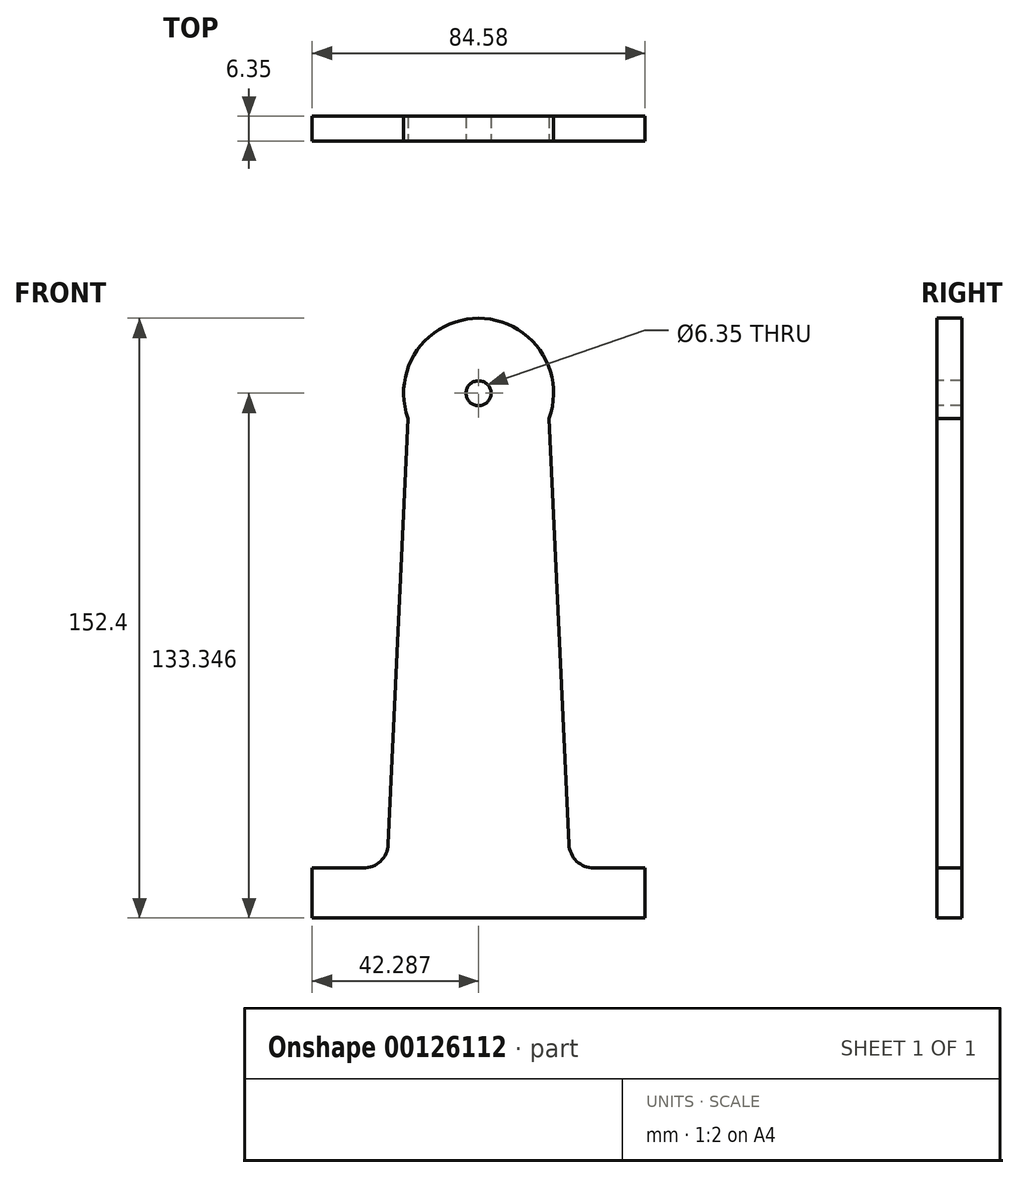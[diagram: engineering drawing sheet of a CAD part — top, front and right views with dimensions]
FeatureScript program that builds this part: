
annotation { "Feature Type Name" : "Feature", "Feature Type Description" : "" }
export const myFeature = defineFeature(function(context is Context, id is Id, definition is map)
    precondition{}
    {
        {
            var Q0;
            Q0=qCreatedBy(makeId("Front.planeOp"),FACE);
            var sketch = newSketch(context, id + "F0", { "sketchPlane" : qUnion([Q0])});
            skLineSegment(sketch, "E0", {"start": v(-71.6, -84.21) * mm, "end": v(12.99, -84.21) * mm});
            skLineSegment(sketch, "E1", {"start": v(12.99, -84.21) * mm, "end": v(12.99, -71.51) * mm});
            skLineSegment(sketch, "E2", {"start": v(12.99, -71.51) * mm, "end": v(0, -71.51) * mm});
            skLineSegment(sketch, "E3", {"start": v(-71.6, -84.21) * mm, "end": v(-71.6, -71.51) * mm});
            skLineSegment(sketch, "E4", {"start": v(-71.6, -71.51) * mm, "end": v(-58.6, -71.51) * mm});
            skPoint(sketch, "E5.endSnap0", {"position": v(-29.3, -84.21) * mm});
            skLineSegment(sketch, "E6", {"start": v(-29.3, -84.21) * mm, "end": v(-29.3, 49.14) * mm, "construction": true});
            skCircle(sketch, "E7", {"center": v(-29.3, 49.14) * mm, "radius": 19.05 * mm});
            skLineSegment(sketch, "E8", {"start": v(-29.3, 49.14) * mm, "end": v(-29.3, 68.19) * mm, "construction": true});
            skLineSegment(sketch, "E9", {"start": v(-6.34, -65.46) * mm, "end": v(-11.36, 42.74) * mm});
            skLineSegment(sketch, "E10", {"start": v(-52.26, -65.46) * mm, "end": v(-47.25, 42.74) * mm});
            skPoint(sketch, "E11.visualSharp", {"position": v(-52.54, -71.51) * mm});
            skArc(sketch, "E11.filletArc", {"start": v(-58.6, -71.51) * mm, "mid": v(-54.22, -69.76) * mm, "end": v(-52.26, -65.46) * mm});
            skPoint(sketch, "E12.visualSharp", {"position": v(-6.06, -71.51) * mm});
            skArc(sketch, "E12.filletArc", {"start": v(-6.34, -65.46) * mm, "mid": v(-4.38, -69.76) * mm, "end": v(0, -71.51) * mm});
            skCircle(sketch, "E13", {"center": v(-29.3, 49.14) * mm, "radius": 3.18 * mm});
            skSolve(sketch);
        }
        {
            var Q0;
            Q0=makeQuery(id+"F0.imprint","IMPRINT",FACE,{"disambiguationData":[TD([[makeQuery(id+"F0.imprint","IMPRINT",EDGE,{"derivedFrom":sQuery(id+"F0.wireOp",EDGE,"E0")}),1.0]])]});
            var Q1;
            Q1=makeQuery(id+"F0.imprint","IMPRINT",FACE,{"disambiguationData":[TD([[makeQuery(id+"F0.imprint","IMPRINT",EDGE,{"derivedFrom":sQuery(id+"F0.wireOp",EDGE,"E13")}),-1.0]])]});
            extrude(context, id + "F1", {"entities" : qUnion([Q0, Q1]), "oppositeDirection" : true, "depth" : 6.35 * mm});
        }
    });
